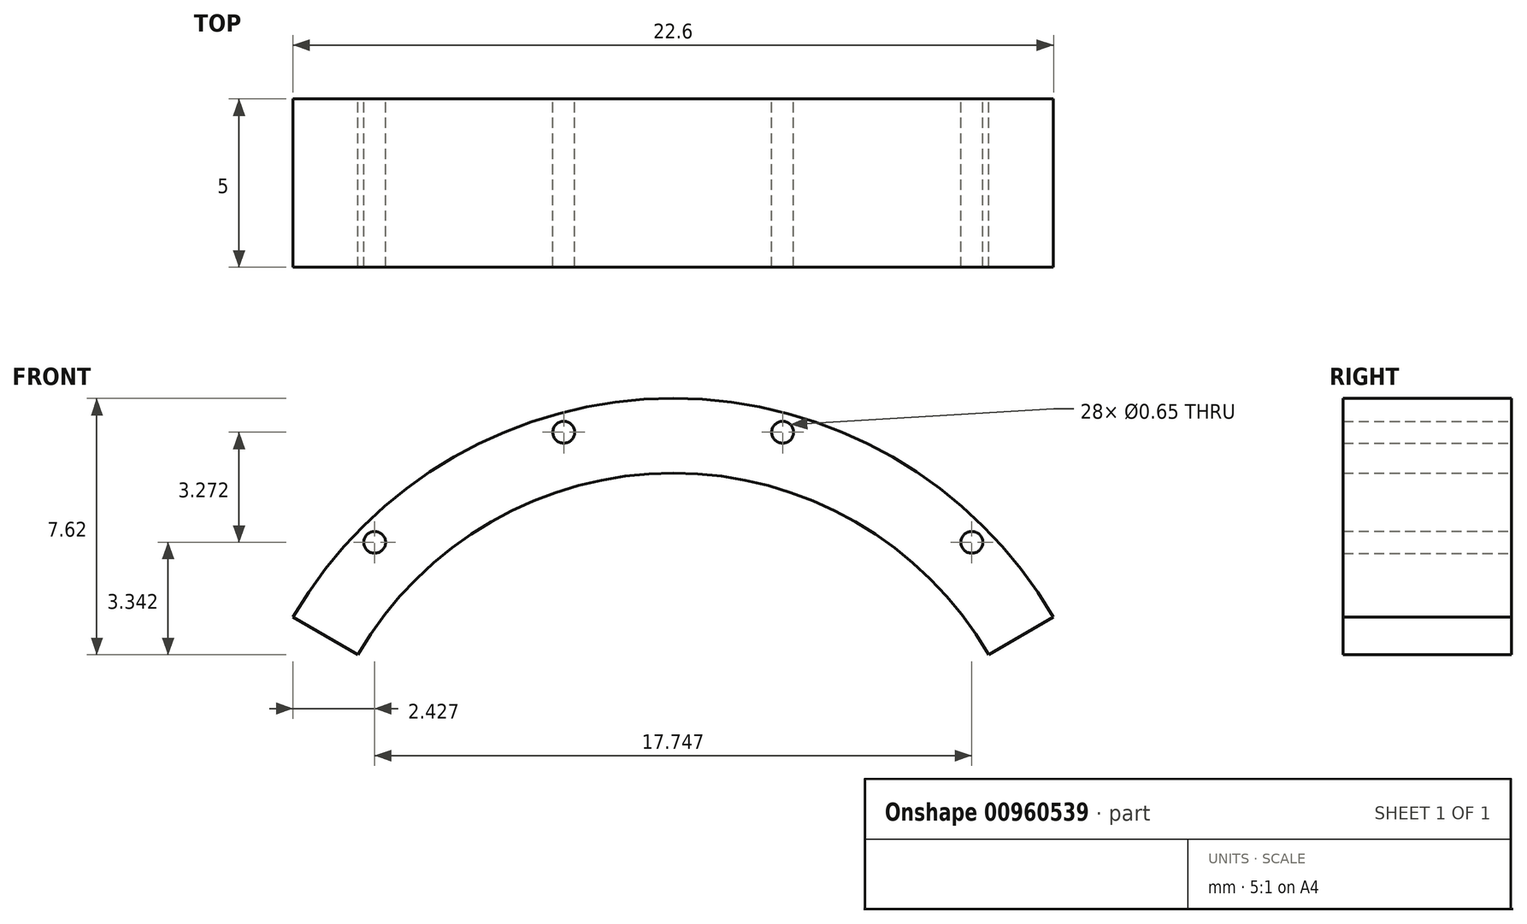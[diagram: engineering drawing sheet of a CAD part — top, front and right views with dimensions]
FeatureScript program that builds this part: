
annotation { "Feature Type Name" : "Feature", "Feature Type Description" : "" }
export const myFeature = defineFeature(function(context is Context, id is Id, definition is map)
    precondition{}
    {
        {
            var Q0;
            Q0=qCreatedBy(makeId("Front.planeOp"),FACE);
            var sketch = newSketch(context, id + "F0", { "sketchPlane" : qUnion([Q0])});
            skLineSegment(sketch, "E0", {"start": v(-9.38, -3.81) * mm, "end": v(-11.3, -2.7) * mm});
            skArc(sketch, "E1", {"start": v(-11.3, -2.7) * mm, "mid": v(0, 3.81) * mm, "end": v(11.3, -2.7) * mm});
            skLineSegment(sketch, "E2", {"start": v(11.3, -2.7) * mm, "end": v(9.38, -3.81) * mm});
            skArc(sketch, "E3", {"start": v(9.38, -3.8) * mm, "mid": v(0, 1.6) * mm, "end": v(-9.38, -3.8) * mm});
            skCircle(sketch, "E4", {"center": v(-3.25, 2.8) * mm, "radius": 0.33 * mm});
            skCircle(sketch, "E5", {"center": v(3.25, 2.8) * mm, "radius": 0.33 * mm});
            skCircle(sketch, "E6", {"center": v(-8.87, -0.47) * mm, "radius": 0.33 * mm});
            skCircle(sketch, "E7", {"center": v(8.87, -0.47) * mm, "radius": 0.33 * mm});
            skSolve(sketch);
        }
        {
            var Q0;
            Q0=makeQuery(id+"F0.imprint","IMPRINT",FACE,{"disambiguationData":[TD([[makeQuery(id+"F0.imprint","IMPRINT",EDGE,{"derivedFrom":sQuery(id+"F0.wireOp",EDGE,"E0")}),-1.0]])]});
            extrude(context, id + "F1", {"entities" : qUnion([Q0]), "depth" : 5 * mm, "offsetDistance" : 25 * mm});
        }
    });
